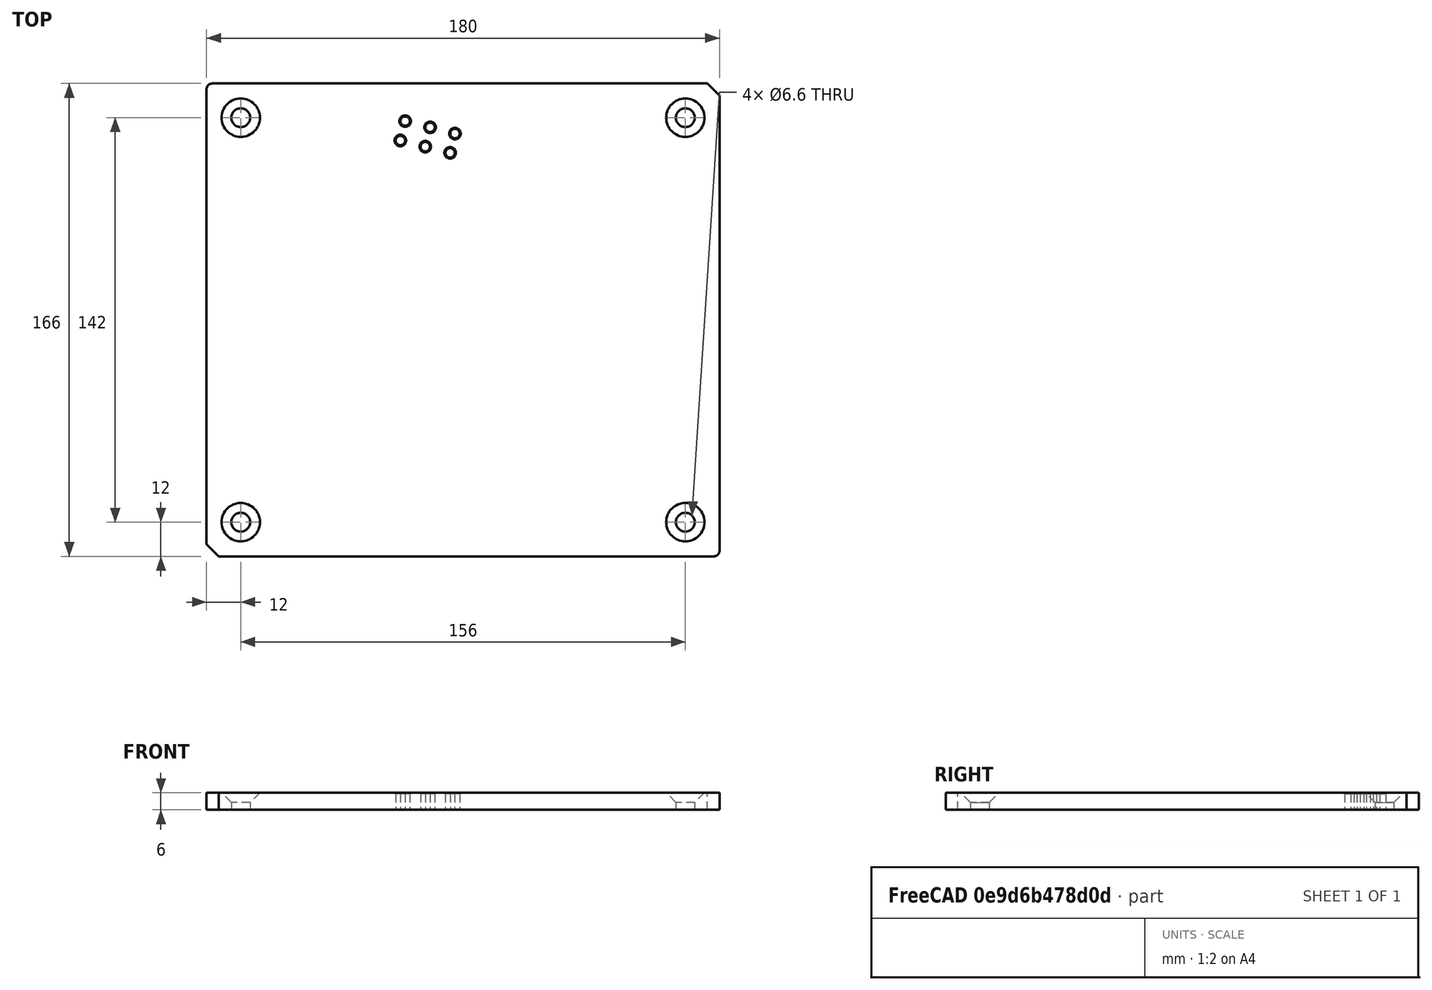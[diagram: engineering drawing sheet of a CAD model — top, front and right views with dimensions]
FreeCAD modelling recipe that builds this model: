
FCSTD DOCUMENT  (FreeCAD 0.19R24267 (Git))
Label: Again
License: All rights reserved
LicenseURL: http://en.wikipedia.org/wiki/All_rights_reserved
objects: Sketcher::SketchObject×3, PartDesign::Hole×2, Spreadsheet::Sheet×1, PartDesign::Pad×1, PartDesign::Body×1
note: 10 computed .brp shape members not serialized (recipe doc carries the construction recipe); baked Part::Feature solids carry a one-line shape summary decoded from their .brp

FEATURE [Sketcher::SketchObject] Sketch
  FullyConstrained = true
  MapMode = 5
  Support = -> [XY_Plane]
  expr: Constraints[14] = <<Parameters>>.FW_1
  expr: Constraints[32] = <<Parameters>>.RK_1
  expr: Constraints[43] = <<Parameters>>.KX_6
  expr: Constraints[44] = <<Parameters>>.KY_6
  sketch-geometry (16):
    g0: LineSegment StartX=2.76674e-11 StartY=2.1323e-12 StartZ=0 EndX=178 EndY=2.1323e-12 EndZ=0
    g1: LineSegment StartX=180 StartY=2 StartZ=0 EndX=180 EndY=166 EndZ=0
    g2: LineSegment StartX=180 StartY=166 StartZ=0 EndX=2.00001 EndY=166 EndZ=0
    g3: LineSegment StartX=2.76674e-11 StartY=164 StartZ=0 EndX=2.76674e-11 EndY=2.1316e-12 EndZ=0
    g4: LineSegment StartX=0 StartY=4.24264 StartZ=0 EndX=4.24264 EndY=0 EndZ=0
    g5: LineSegment StartX=175.757 StartY=166 StartZ=0 EndX=180 EndY=161.757 EndZ=0
    g6: LineSegment StartX=0 StartY=4.24264 StartZ=0 EndX=2.76674e-11 EndY=164 EndZ=0
    g7: LineSegment StartX=2.00001 StartY=166 StartZ=0 EndX=175.757 EndY=166 EndZ=0
    g8: LineSegment StartX=180 StartY=161.757 StartZ=0 EndX=180 EndY=2 EndZ=0
    g9: LineSegment StartX=178 StartY=2.1323e-12 StartZ=0 EndX=4.24264 EndY=0 EndZ=0
    g10: ArcOfCircle CenterX=178 CenterY=2 CenterZ=0 NormalX=0 NormalY=0 NormalZ=1 AngleXU=0 Radius=2 StartAngle=4.71239 EndAngle=6.28319
    g11: ArcOfCircle CenterX=2 CenterY=164 CenterZ=0 NormalX=0 NormalY=0 NormalZ=1 AngleXU=0 Radius=2 StartAngle=1.57079 EndAngle=3.14159
    g12: LineSegment StartX=2.76674e-11 StartY=164 StartZ=0 EndX=0 EndY=166 EndZ=0
    g13: LineSegment StartX=0 StartY=166 StartZ=0 EndX=2.00001 EndY=166 EndZ=0
    g14: LineSegment StartX=178 StartY=2.1323e-12 StartZ=0 EndX=180 EndY=0 EndZ=0
    g15: LineSegment StartX=180 StartY=2 StartZ=0 EndX=180 EndY=0 EndZ=0
  constraints (45):
    c: Coincident(g1,g2)
    c: Coincident(g3,g0)
    c: Horizontal(g0)
    c: Horizontal(g2)
    c: Vertical(g1)
    c: Vertical(g3)
    c: Coincident(g0,g-1)
    c: PointOnObject(g4,g3)
    c: PointOnObject(g4,g0)
    c: PointOnObject(g5,g2)
    c: PointOnObject(g5,g1)
    c: Equal(g4,g5)
    c: Angle(g4,g3) = 2.35619
    c: Angle(g5,g1) = 2.35619
    c: Distance(g5) = 6
    c: Coincident(g6,g4)
    c: Coincident(g6,g3)
    c: Coincident(g7,g2)
    c: Coincident(g7,g5)
    c: Coincident(g8,g5)
    c: Coincident(g8,g1)
    c: Coincident(g9,g0)
    c: Coincident(g9,g4)
    c: Tangent(g10,g9)
    c: Tangent(g8,g10)
    c: Coincident(g9,g10)
    c: Coincident(g10,g8)
    c: Tangent(g11,g7)
    c: Tangent(g6,g11)
    c: Equal(g10,g11)
    c: Coincident(g11,g7)
    c: Coincident(g11,g6)
    c: Radius(g10) = 2
    c: Coincident(g12,g6)
    c: PointOnObject(g12,g-2)
    c: Coincident(g13,g12)
    c: Coincident(g13,g7)
    c: Horizontal(g13)
    c: Coincident(g14,g9)
    c: PointOnObject(g14,g-1)
    c: Coincident(g15,g8)
    c: Coincident(g15,g14)
    c: Vertical(g15)
    c: DistanceX(g-1,g14) = 180
    c: DistanceY(g-1,g12) = 166
FEATURE [Spreadsheet::Sheet] Spreadsheet001  label="Parameters"
  cells = A1=D_1; B1(D_1)=27; A2=KAT; B2(KAT)=14; A3=KAT_2; B3(KAT_2)=28; A4=KPX; B4(KPX)=69; A5=KPY; B5(KPY)=45; A6=D_2; B6(D_2)=39; A7=RKK_1; B7(RKK_1)=6; A8=KOX; B8(KOX)=53; A9=KOY; B9(KOY)=53; A10=WX_1; B10(WX_1)=106; A11=WX_2; B11(WX_2)=136; A12=WY_1; B12(WY_1)=106; A13=RW_1; B13(RW_1)=6; A14=RW_2; B14(RW_2)=14; A15=RW_3; B15(RW_3)=27; A16=RW_4; B16(RW_4)=6; A17=RW_5; B17(RW_5)=6; A18=RW_6; B18(RW_6)=13; A19=FW_1; B19(FW_1)=6; A20=FW_2; B20(FW_2)=5.5; A21=KX_1; B21(KX_1)=12; A22=KX_2; B22(KX_2)=17; A23=KX_3; B23(KX_3)=68; A24=KX_4; B24(KX_4)=139; A25=KX_5; B25(KX_5)=168; A26=KX_6; B26(KX_6)=180; A27=KY_1; B27(KY_1)=12; A28=KY_2; B28(KY_2)=38; A29=KY_3; B29(KY_3)=109; A30=KY_4; B30(KY_4)=146; A31=KY_5; B31(KY_5)=154; A32=KY_6; B32(KY_6)=166; A33=FK_1; B33(FK_1)=2; A34=RK_1; B34(RK_1)=2; A35=H_1; B35(H_1)=12; A36=H_2; B36(H_2)=18; A37=KH_1; B37(KH_1)=10; A38=KH_2; B38(KH_2)=6; A39=OTWX_1; B39(OTWX_1)=9; A40=OTWY_1; B40(OTWY_1)=7; A41=OTWY_2; B41(OTWY_2)=14; A42=GOTW_1; B42(GOTW_1)=14; A43=GOTW_2; B43(GOTW_2)=10; A44=WY_1_1; B44(WY_1_1)=19.0787840283389
FEATURE [PartDesign::Pad] Pad
  Direction = (1,1,1)
  Length = 6
  Length2 = 100
  Profile = -> Sketch
  Type = 0
  expr: Length = <<Parameters>>.H_2 - <<Parameters>>.H_1
FEATURE [Sketcher::SketchObject] Sketch001
  FullyConstrained = true
  MapMode = 5
  Placement = pos=(0,0,6) rot=(0,0,1;0rad)
  Support = -> [Pad]
  expr: Constraints[18] = <<Parameters>>.KX_1
  expr: Constraints[19] = <<Parameters>>.KY_1
  expr: Constraints[20] = <<Parameters>>.KX_5 - <<Parameters>>.KX_1
  expr: Constraints[21] = <<Parameters>>.KY_5 - <<Parameters>>.KY_1
  sketch-geometry (12):
    g0: LineSegment StartX=12 StartY=12 StartZ=0 EndX=168 EndY=12 EndZ=0
    g1: LineSegment StartX=168 StartY=12 StartZ=0 EndX=168 EndY=154 EndZ=0
    g2: LineSegment StartX=168 StartY=154 StartZ=0 EndX=12 EndY=154 EndZ=0
    g3: LineSegment StartX=12 StartY=154 StartZ=0 EndX=12 EndY=12 EndZ=0
    g4: LineSegment StartX=0 StartY=0 StartZ=0 EndX=12 EndY=0 EndZ=0
    g5: LineSegment StartX=12 StartY=0 StartZ=0 EndX=12 EndY=12 EndZ=0
    g6: LineSegment StartX=12 StartY=12 StartZ=0 EndX=0 EndY=12 EndZ=0
    g7: LineSegment StartX=0 StartY=12 StartZ=0 EndX=0 EndY=0 EndZ=0
    g8: Circle CenterX=12 CenterY=154 CenterZ=0 NormalX=0 NormalY=0 NormalZ=1 AngleXU=0 Radius=6.6
    g9: Circle CenterX=168 CenterY=154 CenterZ=0 NormalX=0 NormalY=0 NormalZ=1 AngleXU=0 Radius=6.6
    g10: Circle CenterX=168 CenterY=12 CenterZ=0 NormalX=0 NormalY=0 NormalZ=1 AngleXU=0 Radius=6.6
    g11: Circle CenterX=12 CenterY=12 CenterZ=0 NormalX=0 NormalY=0 NormalZ=1 AngleXU=0 Radius=6.6
  constraints (30):
    c: Coincident(g0,g1)
    c: Coincident(g1,g2)
    c: Coincident(g2,g3)
    c: Coincident(g3,g0)
    c: Horizontal(g0)
    c: Horizontal(g2)
    c: Vertical(g1)
    c: Vertical(g3)
    c: Coincident(g4,g5)
    c: Coincident(g5,g6)
    c: Coincident(g6,g7)
    c: Coincident(g7,g4)
    c: Horizontal(g4)
    c: Horizontal(g6)
    c: Vertical(g5)
    c: Vertical(g7)
    c: Coincident(g4,g-1)
    c: Coincident(g5,g0)
    c: DistanceX(g4,g4) = 12
    c: DistanceY(g7,g7) = 12
    c: DistanceX(g0,g0) = 156
    c: DistanceY(g3,g3) = 142
    c: Coincident(g8,g2)
    c: Coincident(g9,g1)
    c: Coincident(g10,g0)
    c: Coincident(g11,g0)
    c: Equal(g11,g8)
    c: Equal(g8,g9)
    c: Equal(g9,g10)
    c: Radius(g9) = 6.6
FEATURE [PartDesign::Hole] Hole
  BaseFeature = -> Pad
  Depth = 25
  DepthType = 0
  Diameter = 6.6
  DrillForDepth = false
  DrillPoint = 1
  DrillPointAngle = 90
  HoleCutCountersinkAngle = 90
  HoleCutCustomValues = false
  HoleCutDepth = 0
  HoleCutDiameter = 13.44
  HoleCutType = 2
  ModelActualThread = false
  Profile = -> Sketch001
  Tapered = false
  TaperedAngle = 90
  ThreadAngle = 60
  ThreadClass = 0
  ThreadCutOffInner = 0.0270633
  ThreadCutOffOuter = 0.0541266
  ThreadDirection = 0
  ThreadFit = 0
  ThreadPitch = 0.25
  ThreadSize = 0
  ThreadType = 0
  Threaded = false
FEATURE [Sketcher::SketchObject] Sketch002
  ExternalGeometry = -> [Hole]
  FullyConstrained = true
  MapMode = 5
  Placement = pos=(0,0,6) rot=(0,0,1;0rad)
  Support = -> [Hole]
  expr: Constraints[24] = <<Parameters>>.KAT
  expr: Constraints[37] = <<Parameters>>.KX_3
  expr: Constraints[38] = <<Parameters>>.KY_4
  expr: Constraints[39] = <<Parameters>>.OTWY_1
  expr: Constraints[41] = <<Parameters>>.OTWX_1
  sketch-geometry (17):
    g0: LineSegment StartX=0 StartY=0 StartZ=0 EndX=68 EndY=0 EndZ=0
    g1: LineSegment StartX=68 StartY=0 StartZ=0 EndX=68 EndY=146 EndZ=0
    g2: LineSegment StartX=68 StartY=146 StartZ=0 EndX=0 EndY=146 EndZ=0
    g3: LineSegment StartX=0 StartY=146 StartZ=0 EndX=0 EndY=0 EndZ=0
    g4: LineSegment StartX=69.6935 StartY=152.792 StartZ=0 EndX=78.4261 EndY=150.615 EndZ=0
    g5: LineSegment StartX=78.4261 StartY=150.615 StartZ=0 EndX=87.1588 EndY=148.437 EndZ=0
    g6: LineSegment StartX=87.1588 StartY=148.437 StartZ=0 EndX=85.4653 EndY=141.645 EndZ=0
    g7: LineSegment StartX=85.4653 StartY=141.645 StartZ=0 EndX=76.7327 EndY=143.823 EndZ=0
    g8: LineSegment StartX=76.7327 StartY=143.823 StartZ=0 EndX=68 EndY=146 EndZ=0
    g9: LineSegment StartX=76.7327 StartY=143.823 StartZ=0 EndX=78.4261 EndY=150.615 EndZ=0
    g10: LineSegment StartX=68 StartY=146 StartZ=0 EndX=69.6935 EndY=152.792 EndZ=0
    g11: Circle CenterX=69.6935 CenterY=152.792 CenterZ=0 NormalX=0 NormalY=0 NormalZ=1 AngleXU=0 Radius=1.65
    g12: Circle CenterX=78.4261 CenterY=150.615 CenterZ=0 NormalX=0 NormalY=0 NormalZ=1 AngleXU=0 Radius=1.65
    g13: Circle CenterX=87.1588 CenterY=148.437 CenterZ=0 NormalX=0 NormalY=0 NormalZ=1 AngleXU=0 Radius=1.65
    g14: Circle CenterX=68 CenterY=146 CenterZ=0 NormalX=0 NormalY=0 NormalZ=1 AngleXU=0 Radius=1.65
    g15: Circle CenterX=76.7327 CenterY=143.823 CenterZ=0 NormalX=0 NormalY=0 NormalZ=1 AngleXU=0 Radius=1.65
    g16: Circle CenterX=85.4653 CenterY=141.645 CenterZ=0 NormalX=0 NormalY=0 NormalZ=1 AngleXU=0 Radius=1.65
  constraints (42):
    c: Coincident(g0,g1)
    c: Coincident(g1,g2)
    c: Coincident(g2,g3)
    c: Coincident(g3,g0)
    c: Horizontal(g0)
    c: Horizontal(g2)
    c: Vertical(g1)
    c: Vertical(g3)
    c: Coincident(g0,g-1)
    c: Coincident(g5,g4)
    c: Coincident(g7,g6)
    c: Coincident(g8,g7)
    c: Coincident(g8,g1)
    c: Coincident(g9,g7)
    c: Coincident(g9,g4)
    c: Coincident(g10,g1)
    c: Coincident(g10,g4)
    c: Perpendicular(g6,g7)
    c: Perpendicular(g6,g5)
    c: Perpendicular(g4,g9)
    c: Perpendicular(g10,g8)
    c: Perpendicular(g9,g7)
    c: Perpendicular(g10,g4)
    c: Coincident(g6,g5)
    c: Angle(g4,g-3) = 0.244346
    c: Equal(g4,g5)
    c: Coincident(g11,g4)
    c: Coincident(g12,g4)
    c: Coincident(g13,g5)
    c: Coincident(g14,g1)
    c: Coincident(g15,g7)
    c: Coincident(g16,g6)
    c: Equal(g16,g13)
    c: Equal(g13,g12)
    c: Equal(g12,g15)
    c: Equal(g15,g14)
    c: Equal(g14,g11)
    c: DistanceX(g0,g0) = 68
    c: DistanceY(g-1,g2) = 146
    c: Distance(g6) = 7
    c: Diameter(g11) = 3.3
    c: Distance(g4) = 9
FEATURE [PartDesign::Hole] Hole001
  BaseFeature = -> Hole
  Depth = 25
  DepthType = 1
  Diameter = 3.3
  DrillForDepth = false
  DrillPoint = 1
  DrillPointAngle = 90
  HoleCutCountersinkAngle = 90
  HoleCutCustomValues = false
  HoleCutDepth = 0
  HoleCutDiameter = 4.05
  HoleCutType = 2
  ModelActualThread = false
  Profile = -> Sketch002
  Tapered = false
  TaperedAngle = 90
  ThreadAngle = 60
  ThreadClass = 0
  ThreadCutOffInner = 0.0757772
  ThreadCutOffOuter = 0.151554
  ThreadDirection = 0
  ThreadFit = 0
  ThreadPitch = 0.7
  ThreadSize = 11
  ThreadType = 1
  Threaded = true
FEATURE [PartDesign::Body] Body
  Group = -> [Sketch,Pad,Sketch001,Hole,Sketch002,Hole001]
  Origin = -> Origin
  Tip = -> Hole001
